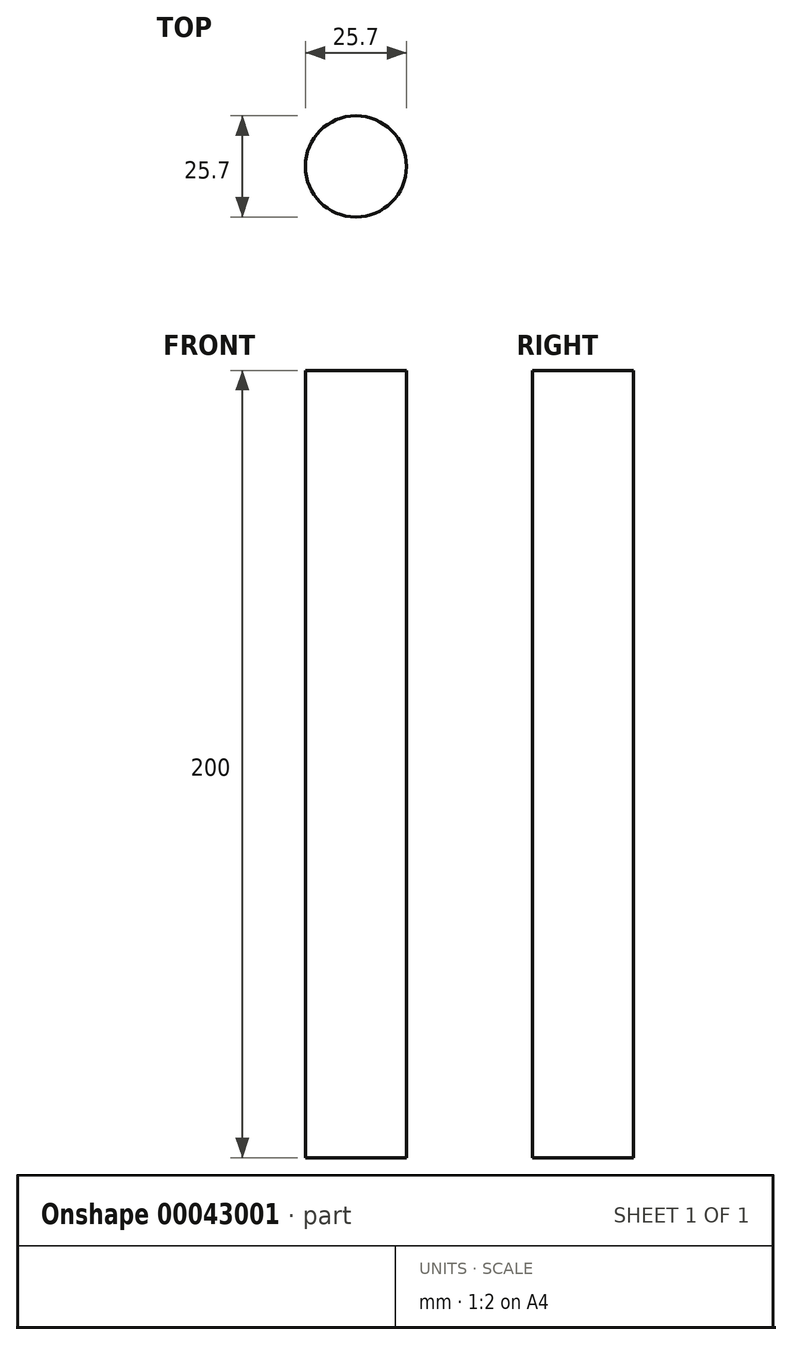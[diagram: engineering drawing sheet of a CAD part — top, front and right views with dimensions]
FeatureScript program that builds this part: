
annotation { "Feature Type Name" : "Feature", "Feature Type Description" : "" }
export const myFeature = defineFeature(function(context is Context, id is Id, definition is map)
    precondition{}
    {
        {
            var Q0;
            Q0=qCreatedBy(makeId("Top.planeOp"),FACE);
            var sketch = newSketch(context, id + "F0", { "sketchPlane" : qUnion([Q0])});
            skCircle(sketch, "E0", {"center": v(0, 0) * mm, "radius": 12.85 * mm});
            skSolve(sketch);
        }
        {
            var Q0;
            Q0=makeQuery(id+"F0.imprint","IMPRINT",FACE,{"disambiguationData":[TD([[makeQuery(id+"F0.imprint","IMPRINT",EDGE,{"derivedFrom":sQuery(id+"F0.wireOp",EDGE,"E0")}),1.0]])]});
            extrude(context, id + "F1", {"entities" : qUnion([Q0]), "depth" : 200 * mm});
        }
    });
